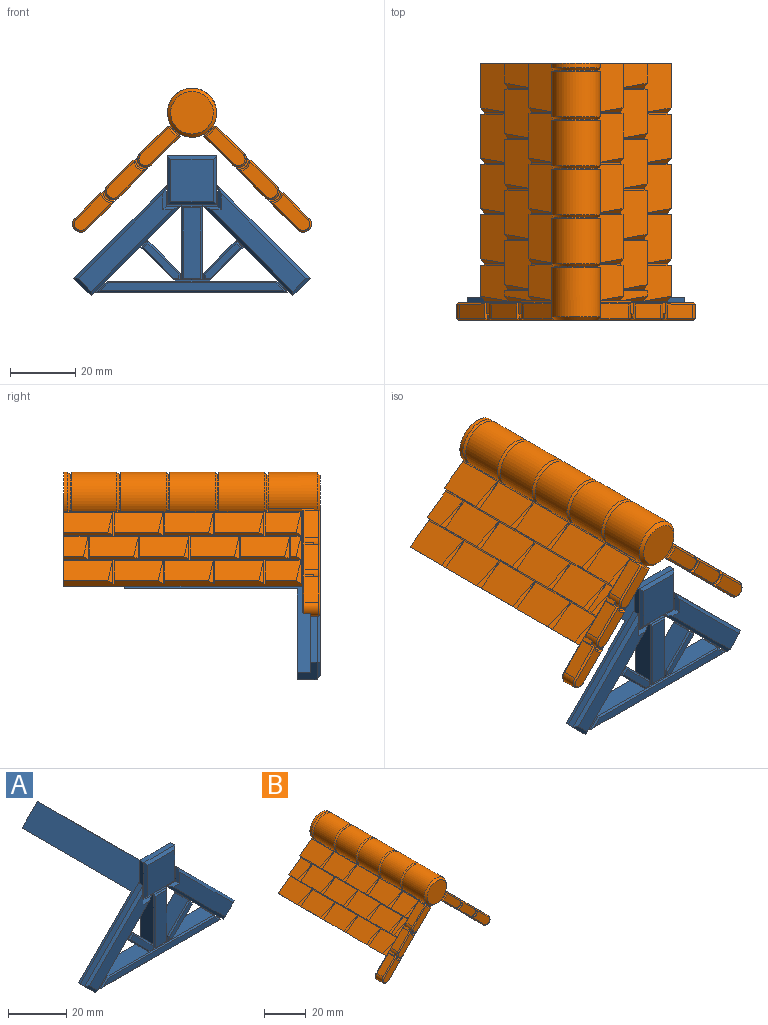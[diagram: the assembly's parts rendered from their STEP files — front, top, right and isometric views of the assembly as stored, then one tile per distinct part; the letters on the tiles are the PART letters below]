
ASSEMBLY  parts=2 mates=1
PART A: 105 faces, bbox 72.4x60x42.8 mm
  f0: plane 6x5.31mm, normal (-0.71,0,-0.71), area 27.5mm2, adj f2,f11,f12,f67,f70,f78
  f1: plane 4.4x0.4mm, normal (0,-1,0), area 1.7mm2, adj f4,f13,f50,f70
  f2: plane 66.14x27.77mm, normal (0,1,0), area 631.8mm2, adj f0,f4,f12,f17,f18,f26,f28,f31
  f3: plane 0.4x0.01mm, normal (0,1,0), area 0mm2, adj f4,f26,f50,f51
  f4: plane 59x15mm, normal (0,0,-1), area 826.6mm2, adj f1,f2,f3,f5,f7,f9,f10,f28
  f5: plane 15x2mm, normal (1,0,0), area 30mm2, adj f4,f6,f68,f82
  f6: plane 15x2mm, normal (0,0,1), area 30mm2, adj f5,f7,f68,f84
  f7: plane 15x2mm, normal (-1,0,0), area 30mm2, adj f4,f6,f68,f85
  f8: plane 13x13mm, normal (0,-1,0), area 169mm2, adj f82,f83,f84,f85
  f9: plane 6.2x0.4mm, normal (0,-1,0), area 2.5mm2, adj f4,f25,f26,f28
  f10: plane 4.4x0.4mm, normal (0,-1,0), area 1.7mm2, adj f4,f21,f54,f69
  f11: plane 28.28x28.28mm, normal (-0.71,0,0.71), area 80mm2, adj f0,f14,f67,f77
  f12: plane 27.37x27.37mm, normal (0.71,0,-0.71), area 207.4mm2, adj f0,f2,f13,f16,f23,f33,f49,f50
  f13: plane 4.4x2mm, normal (0,0,1), area 8.8mm2, adj f1,f12,f14,f81
  f14: plane 6.23x2mm, normal (1,0,0), area 12.5mm2, adj f11,f13,f67,f79
  f15: plane 29.77x28.86mm, normal (0,-1,0), area 191mm2, adj f77,f78,f79,f80,f81
  f16: plane 1.72x1.72mm, normal (0,-1,0), area 0.8mm2, adj f12,f39,f49,f60
  f17: plane 27.37x27.37mm, normal (-0.71,0,-0.71), area 206.4mm2, adj f2,f18,f21,f24,f42,f54,f55,f57
  f18: plane 6x5.31mm, normal (0.71,0,-0.71), area 25.8mm2, adj f2,f17,f19,f69,f71,f76,f86
  f19: plane 28.28x28.28mm, normal (0.71,0,0.71), area 80mm2, adj f18,f20,f71,f74
  f20: plane 6.23x2mm, normal (-1,0,0), area 12.5mm2, adj f19,f21,f71,f72
  f21: plane 4.4x2mm, normal (0,0,1), area 8.8mm2, adj f10,f17,f20,f73
  f22: plane 29.77x28.86mm, normal (0,-1,0), area 191mm2, adj f72,f73,f74,f75,f76
  f23: plane 3.98x3.41mm, normal (0,-1,0), area 1.7mm2, adj f12,f32,f33,f58,f59
  f24: plane 3.26x2.7mm, normal (0,-1,0), area 1.5mm2, adj f17,f34,f61,f63
  f25: plane 6.2x2.5mm, normal (0,0,1), area 15.5mm2, adj f9,f26,f28,f101
  f26: plane 22.91x6.5mm, normal (-1,0,0), area 141.2mm2, adj f2,f3,f9,f25,f27,f30,f51,f52
  f27: plane 6.2x2.5mm, normal (0,0,-1), area 15.5mm2, adj f26,f28,f30,f104
  f28: plane 22.9x6.5mm, normal (1,0,0), area 141.1mm2, adj f2,f4,f9,f25,f27,f30,f53,f103
  f29: plane 21.5x5.2mm, normal (0,-1,0), area 111.8mm2, adj f101,f102,f103,f104
  f30: plane 10.72x2.4mm, normal (0,-1,0), area 5.6mm2, adj f26,f27,f28,f31,f36,f37,f43,f44
  f31: plane 51.67x6.5mm, normal (0,0,1), area 293mm2, adj f2,f30,f32,f34,f56,f58,f64,f89
  f32: plane 3.41x3.41mm, normal (-0.71,0,0.71), area 12.1mm2, adj f23,f31,f33,f90
  f33: plane 59.06x6mm, normal (0,0,-1), area 352.9mm2, adj f12,f23,f32,f34,f86,f88
  f34: plane 6.5x3.41mm, normal (0.71,0,0.71), area 15.9mm2, adj f2,f24,f31,f33,f61,f63,f86,f87
  f35: plane 56.08x2.41mm, normal (0,-1,0), area 129.5mm2, adj f87,f88,f89,f90
  f36: plane 6.5x2.24mm, normal (0,0,-1), area 7.2mm2, adj f2,f30,f37,f40,f64,f100
  f37: plane 6.5x2mm, normal (1,0,0), area 6.3mm2, adj f2,f30,f36,f38,f52,f99
  f38: plane 9.98x9.98mm, normal (0.71,0,0.71), area 91.7mm2, adj f2,f37,f39,f97
  f39: plane 6.5x2.12mm, normal (-0.71,0,0.71), area 11.3mm2, adj f2,f16,f38,f40,f49,f60,f96
  f40: plane 9.86x9.86mm, normal (-0.71,0,-0.71), area 90.6mm2, adj f2,f36,f39,f98
  f41: plane 10.89x10.77mm, normal (0,-1,0), area 27.6mm2, adj f96,f97,f98,f99,f100
  f42: plane 1.85x1.85mm, normal (0,-1,0), area 0.9mm2, adj f17,f46,f55,f57
  f43: plane 2.5x2mm, normal (-1,0,0), area 5mm2, adj f30,f44,f47,f92
  f44: plane 6.5x2.24mm, normal (0,0,-1), area 7.1mm2, adj f2,f30,f43,f45,f56,f94
  f45: plane 9.86x9.86mm, normal (0.71,0,-0.71), area 90.6mm2, adj f2,f44,f46,f95
  f46: plane 6.5x2.12mm, normal (0.71,0,0.71), area 10.6mm2, adj f2,f42,f45,f47,f55,f57,f93
  f47: plane 9.98x9.98mm, normal (-0.71,0,0.71), area 91.7mm2, adj f2,f43,f46,f62,f91
  f48: plane 10.89x10.77mm, normal (0,-1,0), area 27.6mm2, adj f91,f92,f93,f94,f95
  f49: plane 4x0.27mm, normal (0.71,0,0.71), area 1.5mm2, adj f2,f12,f16,f39
  f50: plane 4x0.41mm, normal (1,0,0), area 1.6mm2, adj f1,f2,f3,f12,f51,f66
  f51: plane 4x0.4mm, normal (0,0,-1), area 1.6mm2, adj f3,f26,f50,f66
  f52: plane 4x0.4mm, normal (0,0,1), area 1.6mm2, adj f2,f26,f30,f37
  f53: plane 4x0.39mm, normal (0,0,1), area 1.6mm2, adj f2,f28,f30,f62
  f54: plane 4x0.4mm, normal (-1,0,0), area 1.6mm2, adj f2,f4,f10,f17
  f55: plane 4x0.27mm, normal (-0.71,0,0.71), area 1.5mm2, adj f2,f17,f42,f46
  f56: plane 4x0.4mm, normal (1,0,0), area 1.6mm2, adj f2,f30,f31,f44
  f57: plane 4x0.27mm, normal (0.71,0,-0.71), area 1.5mm2, adj f2,f17,f42,f46
  f58: plane 4x0.47mm, normal (-0.69,0,0.72), area 2.6mm2, adj f2,f23,f31,f59
  f59: plane 4x0.54mm, normal (0,0,1), area 2.2mm2, adj f2,f12,f23,f58
  f60: plane 4x0.27mm, normal (-0.71,0,-0.71), area 1.5mm2, adj f2,f12,f16,f39
  f61: plane 3.9x0.57mm, normal (0,0,-1), area 2.2mm2, adj f17,f24,f34,f86
  f62: plane 4x0.32mm, normal (-1,0,0.03), area 1.3mm2, adj f2,f30,f47,f53
  f63: plane 4x0.57mm, normal (0,0,1), area 2.3mm2, adj f2,f17,f24,f34
  f64: plane 4x0.4mm, normal (-1,0,0), area 1.6mm2, adj f2,f30,f31,f36
  f65: plane 15x7.5mm, normal (0,1,0), area 56.2mm2, adj f4,f69,f70
  f66: plane 0.4x0.01mm, normal (0,-1,0), area 0mm2, adj f4,f26,f50,f51
  f67: plane 31.4x28.28mm, normal (0,1,0), area 166.4mm2, adj f0,f11,f14,f70
  f68: plane 15x15mm, normal (0,1,0), area 168.7mm2, adj f5,f6,f7,f69,f70
  f69: plane 57x33.07mm, normal (0.71,0,0.71), area 749.2mm2, adj f2,f4,f10,f18,f65,f68,f70,f71
  f70: plane 57x33.07mm, normal (-0.71,0,0.71), area 749.2mm2, adj f0,f1,f2,f4,f65,f67,f68,f69
  f71: plane 31.4x28.28mm, normal (0,1,0), area 166.4mm2, adj f18,f19,f20,f69
  f72: plane 7.23x1mm, normal (-0.71,-0.71,0), area 7.8mm2, adj f20,f22,f73,f74
  f73: plane 5.4x1mm, normal (0,-0.71,0.71), area 5.2mm2, adj f21,f22,f72,f75
  f74: plane 28.28x28.28mm, normal (0.5,-0.71,0.5), area 54.2mm2, adj f19,f22,f72,f76
  f75: plane 27.37x27.37mm, normal (-0.5,-0.71,-0.5), area 52.3mm2, adj f17,f22,f73,f76
  f76: plane 5.31x5.31mm, normal (0.5,-0.71,-0.5), area 9.2mm2, adj f18,f22,f74,f75
  f77: plane 28.28x28.28mm, normal (-0.5,-0.71,0.5), area 54.2mm2, adj f11,f15,f78,f79
  f78: plane 5.31x5.31mm, normal (-0.5,-0.71,-0.5), area 9.2mm2, adj f0,f15,f77,f80
  f79: plane 7.23x1mm, normal (0.71,-0.71,0), area 7.8mm2, adj f14,f15,f77,f81
  f80: plane 27.37x27.37mm, normal (0.5,-0.71,-0.5), area 52.3mm2, adj f12,f15,f78,f81
  f81: plane 5.4x1mm, normal (0,-0.71,0.71), area 5.2mm2, adj f13,f15,f79,f80
  f82: plane 15x1mm, normal (0.71,-0.71,0), area 19.8mm2, adj f5,f8,f83,f84
  f83: plane 15x1mm, normal (0,-0.71,-0.71), area 19.8mm2, adj f4,f8,f82,f85
  f84: plane 15x1mm, normal (0,-0.71,0.71), area 19.8mm2, adj f6,f8,f82,f85
  f85: plane 15x1mm, normal (-0.71,-0.71,0), area 19.8mm2, adj f7,f8,f83,f84
  f86: plane 62.24x1.56mm, normal (0,0.71,-0.71), area 44.9mm2, adj f2,f12,f17,f18,f33,f34,f61
  f87: plane 3.62x3.41mm, normal (0.5,-0.71,0.5), area 2.9mm2, adj f34,f35,f88,f89
  f88: plane 58.49x0.5mm, normal (0,-0.71,-0.71), area 40.5mm2, adj f33,f35,f87,f90
  f89: plane 51.67x0.5mm, normal (0,-0.71,0.71), area 36.4mm2, adj f31,f35,f87,f90
  f90: plane 3.62x3.41mm, normal (-0.5,-0.71,0.5), area 2.9mm2, adj f32,f35,f88,f89
  f91: plane 10.19x9.98mm, normal (-0.5,-0.71,0.5), area 9.7mm2, adj f47,f48,f92,f93
  f92: plane 2x0.5mm, normal (-0.71,-0.71,0), area 1.2mm2, adj f43,f48,f91,f94
  f93: plane 2.12x2.12mm, normal (0.5,-0.71,0.5), area 1.8mm2, adj f46,f48,f91,f95
  f94: plane 2.24x0.5mm, normal (0,-0.71,-0.71), area 1.3mm2, adj f44,f48,f92,f95
  f95: plane 10.06x9.86mm, normal (0.5,-0.71,-0.5), area 9.6mm2, adj f45,f48,f93,f94
  f96: plane 2.12x2.12mm, normal (-0.5,-0.71,0.5), area 1.8mm2, adj f39,f41,f97,f98
  f97: plane 10.19x9.98mm, normal (0.5,-0.71,0.5), area 9.7mm2, adj f38,f41,f96,f99
  f98: plane 10.06x9.86mm, normal (-0.5,-0.71,-0.5), area 9.6mm2, adj f40,f41,f96,f100
  f99: plane 2x0.5mm, normal (0.71,-0.71,0), area 1.2mm2, adj f37,f41,f97,f100
  f100: plane 2.24x0.5mm, normal (0,-0.71,-0.71), area 1.3mm2, adj f36,f41,f98,f99
  f101: plane 6.2x0.5mm, normal (0,-0.71,0.71), area 4mm2, adj f25,f29,f102,f103
  f102: plane 22.5x0.5mm, normal (-0.71,-0.71,0), area 15.6mm2, adj f26,f29,f101,f104
  f103: plane 22.5x0.5mm, normal (0.71,-0.71,0), area 15.6mm2, adj f28,f29,f101,f104
  f104: plane 6.2x0.5mm, normal (0,-0.71,-0.71), area 4mm2, adj f27,f29,f102,f103
PART B: 262 faces, bbox 73x78.5x44 mm
  f0: cylinder r=7.5mm len=15mm, axis (0,1,0), area 460mm2, adj f14,f121,f251,f259
  f1: cylinder r=7.5mm len=15mm, axis (0,1,0), area 460mm2, adj f14,f121,f244,f249
  f2: cylinder r=7.5mm len=15mm, axis (0,1,0), area 460mm2, adj f14,f121,f237,f242
  f3: cylinder r=7.5mm len=15mm, axis (0,1,0), area 460mm2, adj f14,f121,f230,f235
  f4: cylinder r=7.5mm len=15mm, axis (0,1,0), area 43.3mm2, adj f5,f14,f121,f228
  f5: plane 58.17x34.82mm, normal (0,1,0), area 239.8mm2, adj f4,f8,f12,f14,f41,f42,f85,f86
  f6: plane 31.73x30.05mm, normal (0,1,0), area 53.4mm2, adj f8,f9,f14,f16,f35,f39,f40,f104
  f7: cylinder r=2.5mm len=4.5mm, axis (0,1,0), area 27.5mm2, adj f9,f30,f31,f99,f224,f226
  f8: plane 73x1.77mm, normal (-0.71,0,-0.71), area 173.9mm2, adj f5,f6,f14,f47,f52,f57,f60,f65
  f9: cone r=2mm half-angle=45deg, axis (0,-1,0), area 2.5mm2, adj f6,f7,f104,f226
  f10: plane 31.73x30.05mm, normal (0,1,0), area 53.4mm2, adj f12,f13,f15,f121,f139,f143,f144,f207
  f11: cylinder r=2.5mm len=4.5mm, axis (0,1,0), area 27.5mm2, adj f13,f134,f135,f202,f224,f225
  f12: plane 73x1.77mm, normal (0.71,0,-0.71), area 173.9mm2, adj f5,f10,f121,f151,f156,f161,f164,f169
  f13: cone r=2mm half-angle=45deg, axis (0,-1,0), area 2.5mm2, adj f10,f11,f207,f225
  f14: plane 73x22.06mm, normal (-0.71,0,0.71), area 151.6mm2, adj f0,f1,f2,f3,f4,f5,f6,f8
  f15: cylinder r=7.5mm len=15mm, axis (0,1,0), area 503.7mm2, adj f10,f16,f18,f38,f39,f97,f121,f122
  f16: cylinder r=7.5mm len=10.5mm, axis (0,1,0), area 10.7mm2, adj f6,f14,f15,f257
  f17: plane 13x13mm, normal (0,-1,0), area 132.7mm2, adj f97
  f18: plane 3.28x3.19mm, normal (0,-1,0), area 2mm2, adj f15,f19,f38,f39,f118
  f19: cylinder r=8mm len=3.22mm, axis (0,1,0), area 7.2mm2, adj f18,f22,f38,f115,f118,f224
  f20: plane 8.37x8.37mm, normal (-0.71,0,0.71), area 53.3mm2, adj f21,f116,f118,f119
  f21: cylinder r=2.5mm len=4.5mm, axis (0,1,0), area 18.2mm2, adj f20,f22,f29,f37,f40,f114,f120,f224
  f22: plane 8.84x8.84mm, normal (0.71,0,-0.71), area 31.2mm2, adj f19,f21,f113,f224
  f23: plane 11.79x11.79mm, normal (0,-1,0), area 53mm2, adj f113,f114,f115,f116
  f24: plane 7.82x7.82mm, normal (-0.71,0,0.71), area 49.8mm2, adj f25,f108,f110,f111
  f25: cylinder r=2.5mm len=4.5mm, axis (0,1,0), area 18.2mm2, adj f24,f26,f34,f35,f36,f106,f112,f224
  f26: plane 8.84x8.84mm, normal (0.71,0,-0.71), area 31.2mm2, adj f25,f27,f105,f224
  f27: cylinder r=2.73mm len=3.7mm, axis (0,1,0), area 8.4mm2, adj f26,f29,f37,f107,f110,f224
  f28: plane 11.24x11.24mm, normal (0,-1,0), area 48.6mm2, adj f105,f106,f107,f108
  f29: plane 3.67x3.37mm, normal (0,-1,0), area 2.7mm2, adj f21,f27,f37,f40,f110
  f30: plane 7.82x7.82mm, normal (-0.71,0,0.71), area 49.8mm2, adj f7,f101,f103,f104
  f31: plane 8.84x8.84mm, normal (0.71,0,-0.71), area 31.2mm2, adj f7,f32,f98,f224
  f32: cylinder r=2.73mm len=3.7mm, axis (0,1,0), area 8.4mm2, adj f31,f34,f36,f100,f103,f224
  f33: plane 11.24x11.24mm, normal (0,-1,0), area 48.6mm2, adj f98,f99,f100,f101
  f34: plane 3.67x3.37mm, normal (0,-1,0), area 2.7mm2, adj f25,f32,f35,f36,f103
  f35: plane 3.5x1.91mm, normal (-0.71,0,0.71), area 4.4mm2, adj f6,f25,f34,f103,f112
  f36: plane 1x0.54mm, normal (0.71,0,-0.71), area 0.8mm2, adj f25,f32,f34,f224
  f37: plane 1x0.54mm, normal (0.71,0,-0.71), area 0.8mm2, adj f21,f27,f29,f224
  f38: plane 1x0.37mm, normal (0.71,0,-0.71), area 0.5mm2, adj f15,f18,f19,f224
  f39: plane 3.5x0.45mm, normal (-0.71,0,0.71), area 2.2mm2, adj f6,f15,f18,f118
  f40: plane 3.5x1.91mm, normal (-0.71,0,0.71), area 4.4mm2, adj f6,f21,f29,f110,f120
  f41: plane 15x1.06mm, normal (-0.71,0,-0.71), area 21.4mm2, adj f5,f14,f80,f95
  f42: plane 7.5x1.06mm, normal (-0.71,0,-0.71), area 10.1mm2, adj f5,f14,f70,f86
  f43: plane 15x1.06mm, normal (-0.71,0,-0.71), area 21.4mm2, adj f14,f44,f71,f87
  f44: plane 8.13x7.07mm, normal (0,1,0), area 7.5mm2, adj f14,f43,f87
  f45: plane 8.13x7.07mm, normal (0,1,0), area 7.5mm2, adj f14,f46,f94
  f46: plane 15x1.06mm, normal (-0.71,0,-0.71), area 21.4mm2, adj f14,f45,f79,f94
  f47: plane 8.13x7.07mm, normal (0,1,0), area 7.5mm2, adj f8,f14,f84
  f48: plane 8.13x7.07mm, normal (0,1,0), area 7.5mm2, adj f14,f49,f88
  f49: plane 15x1.06mm, normal (-0.71,0,-0.71), area 21.4mm2, adj f14,f48,f72,f88
  f50: plane 8.13x7.07mm, normal (0,1,0), area 7.5mm2, adj f14,f51,f93
  f51: plane 15x1.06mm, normal (-0.71,0,-0.71), area 21.4mm2, adj f14,f50,f78,f93
  f52: plane 8.13x7.07mm, normal (0,1,0), area 7.5mm2, adj f8,f14,f83
  f53: plane 8.13x7.07mm, normal (0,1,0), area 7.5mm2, adj f14,f54,f89
  f54: plane 15x1.06mm, normal (-0.71,0,-0.71), area 21.4mm2, adj f14,f53,f73,f89
  f55: plane 8.13x7.07mm, normal (0,1,0), area 7.5mm2, adj f14,f56,f92
  f56: plane 15x1.06mm, normal (-0.71,0,-0.71), area 21.4mm2, adj f14,f55,f77,f92
  f57: plane 8.13x7.07mm, normal (0,1,0), area 7.5mm2, adj f8,f14,f82
  f58: plane 8.13x7.07mm, normal (0,1,0), area 7.5mm2, adj f14,f59,f90
  f59: plane 15x1.06mm, normal (-0.71,0,-0.71), area 21.4mm2, adj f14,f58,f74,f90
  f60: plane 8.13x7.07mm, normal (0,1,0), area 7.5mm2, adj f8,f14,f81
  f61: plane 8.13x7.07mm, normal (0,1,0), area 7.5mm2, adj f14,f62,f96
  f62: plane 3.1x1.06mm, normal (-0.71,0,-0.71), area 3.5mm2, adj f14,f61,f75,f96
  f63: plane 8.13x7.07mm, normal (0,1,0), area 7.5mm2, adj f14,f64,f91
  f64: plane 11x1.06mm, normal (-0.71,0,-0.71), area 15.4mm2, adj f14,f63,f76,f91
  f65: plane 8.13x7.07mm, normal (-0.5,-0.71,0.5), area 10.6mm2, adj f8,f14,f81
  f66: plane 8.13x7.07mm, normal (-0.5,-0.71,0.5), area 10.6mm2, adj f8,f14,f82
  f67: plane 8.13x7.07mm, normal (-0.5,-0.71,0.5), area 10.6mm2, adj f8,f14,f83
  f68: plane 8.13x7.07mm, normal (-0.5,-0.71,0.5), area 10.6mm2, adj f8,f14,f84
  f69: plane 8.13x7.07mm, normal (-0.5,-0.71,0.5), area 10.6mm2, adj f8,f14,f85
  f70: plane 8.13x7.07mm, normal (-0.5,-0.71,0.5), area 10.6mm2, adj f14,f42,f86
  f71: plane 8.13x7.07mm, normal (-0.5,-0.71,0.5), area 10.6mm2, adj f14,f43,f87
  f72: plane 8.13x7.07mm, normal (-0.5,-0.71,0.5), area 10.6mm2, adj f14,f49,f88
  f73: plane 8.13x7.07mm, normal (-0.5,-0.71,0.5), area 10.6mm2, adj f14,f54,f89
  f74: plane 8.13x7.07mm, normal (-0.5,-0.71,0.5), area 10.6mm2, adj f14,f59,f90
  f75: plane 8.13x7.07mm, normal (-0.5,-0.71,0.5), area 10.6mm2, adj f14,f62,f96
  f76: plane 8.13x7.07mm, normal (-0.5,-0.71,0.5), area 10.6mm2, adj f14,f64,f91
  f77: plane 8.13x7.07mm, normal (-0.5,-0.71,0.5), area 10.6mm2, adj f14,f56,f92
  f78: plane 8.13x7.07mm, normal (-0.5,-0.71,0.5), area 10.6mm2, adj f14,f51,f93
  f79: plane 8.13x7.07mm, normal (-0.5,-0.71,0.5), area 10.6mm2, adj f14,f46,f94
  f80: plane 8.13x7.07mm, normal (-0.5,-0.71,0.5), area 10.6mm2, adj f14,f41,f95
  f81: plane 11x8.13mm, normal (-0.59,0,0.8), area 103.6mm2, adj f8,f14,f60,f65
  f82: plane 15x8.13mm, normal (-0.59,0,0.8), area 144.1mm2, adj f8,f14,f57,f66
  f83: plane 15x8.13mm, normal (-0.59,0,0.8), area 144.1mm2, adj f8,f14,f52,f67
  f84: plane 15x8.13mm, normal (-0.59,0,0.8), area 144.1mm2, adj f8,f14,f47,f68
  f85: plane 15x8.13mm, normal (-0.59,0,0.8), area 144.1mm2, adj f5,f8,f14,f69
  f86: plane 8.13x7.5mm, normal (-0.59,0,0.8), area 68.3mm2, adj f5,f14,f42,f70
  f87: plane 15x8.13mm, normal (-0.59,0,0.8), area 144.1mm2, adj f14,f43,f44,f71
  f88: plane 15x8.13mm, normal (-0.59,0,0.8), area 144.1mm2, adj f14,f48,f49,f72
  f89: plane 15x8.13mm, normal (-0.59,0,0.8), area 144.1mm2, adj f14,f53,f54,f73
  f90: plane 15x8.13mm, normal (-0.59,0,0.8), area 144.1mm2, adj f14,f58,f59,f74
  f91: plane 11x8.13mm, normal (-0.59,0,0.8), area 103.6mm2, adj f14,f63,f64,f76
  f92: plane 15x8.13mm, normal (-0.59,0,0.8), area 144.1mm2, adj f14,f55,f56,f77
  f93: plane 15x8.13mm, normal (-0.59,0,0.8), area 144.1mm2, adj f14,f50,f51,f78
  f94: plane 15x8.13mm, normal (-0.59,0,0.8), area 144.1mm2, adj f14,f45,f46,f79
  f95: plane 15x8.13mm, normal (-0.59,0,0.8), area 144.1mm2, adj f5,f14,f41,f80
  f96: plane 8.13x6.01mm, normal (-0.59,0,0.8), area 23.8mm2, adj f14,f61,f62,f75
  f97: cone r=6.5mm half-angle=45deg, axis (0,1,0), area 62.2mm2, adj f15,f17
  f98: plane 9.19x8.84mm, normal (0.5,-0.71,-0.5), area 8.3mm2, adj f31,f33,f99,f100
  f99: cone r=2mm half-angle=45deg, axis (0,1,0), area 5mm2, adj f7,f33,f98,f101
  f100: cone r=2.73mm half-angle=45deg, axis (0,-1,0), area 3.2mm2, adj f32,f33,f98,f102
  f101: plane 8.18x8.18mm, normal (-0.5,-0.71,0.5), area 7.8mm2, adj f30,f33,f99,f102
  f102: plane 0.85x0.5mm, normal (0.3,-0.4,0.87), area 0.2mm2, adj f100,f101,f103
  f103: plane 5x0.85mm, normal (0.33,0,0.94), area 3.2mm2, adj f30,f32,f34,f35,f102,f104
  f104: plane 8.35x8.18mm, normal (-0.5,0.71,0.5), area 7.9mm2, adj f6,f9,f30,f103
  f105: plane 9.19x8.84mm, normal (0.5,-0.71,-0.5), area 8.3mm2, adj f26,f28,f106,f107
  f106: cone r=2mm half-angle=45deg, axis (0,1,0), area 5mm2, adj f25,f28,f105,f108
  f107: cone r=2.73mm half-angle=45deg, axis (0,-1,0), area 3.2mm2, adj f27,f28,f105,f109
  f108: plane 8.18x8.18mm, normal (-0.5,-0.71,0.5), area 7.8mm2, adj f24,f28,f106,f109
  f109: plane 0.85x0.5mm, normal (0.3,-0.4,0.87), area 0.2mm2, adj f107,f108,f110
  f110: plane 5x0.85mm, normal (0.33,0,0.94), area 3.2mm2, adj f24,f27,f29,f40,f109,f111
  f111: plane 8.35x8.18mm, normal (-0.5,0.71,0.5), area 7.9mm2, adj f6,f24,f110,f112
  f112: cone r=2mm half-angle=45deg, axis (0,-1,0), area 0.7mm2, adj f6,f25,f35,f111
  f113: plane 9.21x8.86mm, normal (0.5,-0.71,-0.5), area 8.6mm2, adj f22,f23,f114,f115
  f114: cone r=2mm half-angle=45deg, axis (0,1,0), area 5mm2, adj f21,f23,f113,f116
  f115: cone r=8mm half-angle=45deg, axis (0,-1,0), area 3mm2, adj f19,f23,f113,f117
  f116: plane 8.72x8.72mm, normal (-0.5,-0.71,0.5), area 8.4mm2, adj f20,f23,f114,f117
  f117: plane 0.78x0.5mm, normal (0.1,-0.53,0.84), area 0.2mm2, adj f115,f116,f118
  f118: plane 5x0.78mm, normal (0.12,0,0.99), area 3.2mm2, adj f18,f19,f20,f39,f117,f119
  f119: plane 9x8.72mm, normal (-0.5,0.71,0.5), area 8.5mm2, adj f6,f20,f118,f120
  f120: cone r=2mm half-angle=45deg, axis (0,-1,0), area 0.7mm2, adj f6,f21,f40,f119
  f121: plane 73x22.06mm, normal (0.71,0,0.71), area 151.6mm2, adj f0,f1,f2,f3,f4,f5,f10,f12
  f122: plane 3.28x3.19mm, normal (0,-1,0), area 2mm2, adj f15,f123,f142,f143,f221
  f123: cylinder r=8mm len=3.22mm, axis (0,1,0), area 7.2mm2, adj f122,f126,f142,f218,f221,f224
  f124: plane 8.37x8.37mm, normal (0.71,0,0.71), area 53.3mm2, adj f125,f219,f221,f222
  f125: cylinder r=2.5mm len=4.5mm, axis (0,1,0), area 18.2mm2, adj f124,f126,f133,f141,f144,f217,f223,f224
  f126: plane 8.84x8.84mm, normal (-0.71,0,-0.71), area 31.2mm2, adj f123,f125,f216,f224
  f127: plane 11.79x11.79mm, normal (0,-1,0), area 53mm2, adj f216,f217,f218,f219
  f128: plane 7.82x7.82mm, normal (0.71,0,0.71), area 49.8mm2, adj f129,f211,f213,f214
  f129: cylinder r=2.5mm len=4.5mm, axis (0,1,0), area 18.2mm2, adj f128,f130,f138,f139,f140,f209,f215,f224
  f130: plane 8.84x8.84mm, normal (-0.71,0,-0.71), area 31.2mm2, adj f129,f131,f208,f224
  f131: cylinder r=2.73mm len=3.7mm, axis (0,1,0), area 8.4mm2, adj f130,f133,f141,f210,f213,f224
  f132: plane 11.24x11.24mm, normal (0,-1,0), area 48.6mm2, adj f208,f209,f210,f211
  f133: plane 3.67x3.37mm, normal (0,-1,0), area 2.7mm2, adj f125,f131,f141,f144,f213
  f134: plane 7.82x7.82mm, normal (0.71,0,0.71), area 49.8mm2, adj f11,f204,f206,f207
  f135: plane 8.84x8.84mm, normal (-0.71,0,-0.71), area 31.2mm2, adj f11,f136,f201,f224
  f136: cylinder r=2.73mm len=3.7mm, axis (0,1,0), area 8.4mm2, adj f135,f138,f140,f203,f206,f224
  f137: plane 11.24x11.24mm, normal (0,-1,0), area 48.6mm2, adj f201,f202,f203,f204
  f138: plane 3.67x3.37mm, normal (0,-1,0), area 2.7mm2, adj f129,f136,f139,f140,f206
  f139: plane 3.5x1.91mm, normal (0.71,0,0.71), area 4.4mm2, adj f10,f129,f138,f206,f215
  f140: plane 1x0.54mm, normal (-0.71,0,-0.71), area 0.8mm2, adj f129,f136,f138,f224
  f141: plane 1x0.54mm, normal (-0.71,0,-0.71), area 0.8mm2, adj f125,f131,f133,f224
  f142: plane 1x0.37mm, normal (-0.71,0,-0.71), area 0.5mm2, adj f15,f122,f123,f224
  f143: plane 3.5x0.45mm, normal (0.71,0,0.71), area 2.2mm2, adj f10,f15,f122,f221
  f144: plane 3.5x1.91mm, normal (0.71,0,0.71), area 4.4mm2, adj f10,f125,f133,f213,f223
  f145: plane 15x1.06mm, normal (0.71,0,-0.71), area 21.4mm2, adj f5,f121,f184,f199
  f146: plane 7.5x1.06mm, normal (0.71,0,-0.71), area 10.1mm2, adj f5,f121,f174,f190
  f147: plane 15x1.06mm, normal (0.71,0,-0.71), area 21.4mm2, adj f121,f148,f175,f191
  f148: plane 8.13x7.07mm, normal (0,1,0), area 7.5mm2, adj f121,f147,f191
  f149: plane 8.13x7.07mm, normal (0,1,0), area 7.5mm2, adj f121,f150,f198
  f150: plane 15x1.06mm, normal (0.71,0,-0.71), area 21.4mm2, adj f121,f149,f183,f198
  f151: plane 8.13x7.07mm, normal (0,1,0), area 7.5mm2, adj f12,f121,f188
  f152: plane 8.13x7.07mm, normal (0,1,0), area 7.5mm2, adj f121,f153,f192
  f153: plane 15x1.06mm, normal (0.71,0,-0.71), area 21.4mm2, adj f121,f152,f176,f192
  f154: plane 8.13x7.07mm, normal (0,1,0), area 7.5mm2, adj f121,f155,f197
  f155: plane 15x1.06mm, normal (0.71,0,-0.71), area 21.4mm2, adj f121,f154,f182,f197
  f156: plane 8.13x7.07mm, normal (0,1,0), area 7.5mm2, adj f12,f121,f187
  f157: plane 8.13x7.07mm, normal (0,1,0), area 7.5mm2, adj f121,f158,f193
  f158: plane 15x1.06mm, normal (0.71,0,-0.71), area 21.4mm2, adj f121,f157,f177,f193
  f159: plane 8.13x7.07mm, normal (0,1,0), area 7.5mm2, adj f121,f160,f196
  f160: plane 15x1.06mm, normal (0.71,0,-0.71), area 21.4mm2, adj f121,f159,f181,f196
  f161: plane 8.13x7.07mm, normal (0,1,0), area 7.5mm2, adj f12,f121,f186
  f162: plane 8.13x7.07mm, normal (0,1,0), area 7.5mm2, adj f121,f163,f194
  f163: plane 15x1.06mm, normal (0.71,0,-0.71), area 21.4mm2, adj f121,f162,f178,f194
  f164: plane 8.13x7.07mm, normal (0,1,0), area 7.5mm2, adj f12,f121,f185
  f165: plane 8.13x7.07mm, normal (0,1,0), area 7.5mm2, adj f121,f166,f200
  f166: plane 3.1x1.06mm, normal (0.71,0,-0.71), area 3.5mm2, adj f121,f165,f179,f200
  f167: plane 8.13x7.07mm, normal (0,1,0), area 7.5mm2, adj f121,f168,f195
  f168: plane 11x1.06mm, normal (0.71,0,-0.71), area 15.4mm2, adj f121,f167,f180,f195
  f169: plane 8.13x7.07mm, normal (0.5,-0.71,0.5), area 10.6mm2, adj f12,f121,f185
  f170: plane 8.13x7.07mm, normal (0.5,-0.71,0.5), area 10.6mm2, adj f12,f121,f186
  f171: plane 8.13x7.07mm, normal (0.5,-0.71,0.5), area 10.6mm2, adj f12,f121,f187
  f172: plane 8.13x7.07mm, normal (0.5,-0.71,0.5), area 10.6mm2, adj f12,f121,f188
  f173: plane 8.13x7.07mm, normal (0.5,-0.71,0.5), area 10.6mm2, adj f12,f121,f189
  f174: plane 8.13x7.07mm, normal (0.5,-0.71,0.5), area 10.6mm2, adj f121,f146,f190
  f175: plane 8.13x7.07mm, normal (0.5,-0.71,0.5), area 10.6mm2, adj f121,f147,f191
  f176: plane 8.13x7.07mm, normal (0.5,-0.71,0.5), area 10.6mm2, adj f121,f153,f192
  f177: plane 8.13x7.07mm, normal (0.5,-0.71,0.5), area 10.6mm2, adj f121,f158,f193
  f178: plane 8.13x7.07mm, normal (0.5,-0.71,0.5), area 10.6mm2, adj f121,f163,f194
  f179: plane 8.13x7.07mm, normal (0.5,-0.71,0.5), area 10.6mm2, adj f121,f166,f200
  f180: plane 8.13x7.07mm, normal (0.5,-0.71,0.5), area 10.6mm2, adj f121,f168,f195
  f181: plane 8.13x7.07mm, normal (0.5,-0.71,0.5), area 10.6mm2, adj f121,f160,f196
  f182: plane 8.13x7.07mm, normal (0.5,-0.71,0.5), area 10.6mm2, adj f121,f155,f197
  f183: plane 8.13x7.07mm, normal (0.5,-0.71,0.5), area 10.6mm2, adj f121,f150,f198
  f184: plane 8.13x7.07mm, normal (0.5,-0.71,0.5), area 10.6mm2, adj f121,f145,f199
  f185: plane 11x8.13mm, normal (0.59,0,0.8), area 103.6mm2, adj f12,f121,f164,f169
  f186: plane 15x8.13mm, normal (0.59,0,0.8), area 144.1mm2, adj f12,f121,f161,f170
  f187: plane 15x8.13mm, normal (0.59,0,0.8), area 144.1mm2, adj f12,f121,f156,f171
  f188: plane 15x8.13mm, normal (0.59,0,0.8), area 144.1mm2, adj f12,f121,f151,f172
  f189: plane 15x8.13mm, normal (0.59,0,0.8), area 144.1mm2, adj f5,f12,f121,f173
  f190: plane 8.13x7.5mm, normal (0.59,0,0.8), area 68.3mm2, adj f5,f121,f146,f174
  f191: plane 15x8.13mm, normal (0.59,0,0.8), area 144.1mm2, adj f121,f147,f148,f175
  f192: plane 15x8.13mm, normal (0.59,0,0.8), area 144.1mm2, adj f121,f152,f153,f176
  f193: plane 15x8.13mm, normal (0.59,0,0.8), area 144.1mm2, adj f121,f157,f158,f177
  f194: plane 15x8.13mm, normal (0.59,0,0.8), area 144.1mm2, adj f121,f162,f163,f178
  f195: plane 11x8.13mm, normal (0.59,0,0.8), area 103.6mm2, adj f121,f167,f168,f180
  f196: plane 15x8.13mm, normal (0.59,0,0.8), area 144.1mm2, adj f121,f159,f160,f181
  f197: plane 15x8.13mm, normal (0.59,0,0.8), area 144.1mm2, adj f121,f154,f155,f182
  f198: plane 15x8.13mm, normal (0.59,0,0.8), area 144.1mm2, adj f121,f149,f150,f183
  f199: plane 15x8.13mm, normal (0.59,0,0.8), area 144.1mm2, adj f5,f121,f145,f184
  f200: plane 8.13x6.01mm, normal (0.59,0,0.8), area 23.8mm2, adj f121,f165,f166,f179
  f201: plane 9.19x8.84mm, normal (-0.5,-0.71,-0.5), area 8.3mm2, adj f135,f137,f202,f203
  f202: cone r=2mm half-angle=45deg, axis (0,1,0), area 5mm2, adj f11,f137,f201,f204
  f203: cone r=2.73mm half-angle=45deg, axis (0,-1,0), area 3.2mm2, adj f136,f137,f201,f205
  f204: plane 8.18x8.18mm, normal (0.5,-0.71,0.5), area 7.8mm2, adj f134,f137,f202,f205
  f205: plane 0.85x0.5mm, normal (-0.3,-0.4,0.87), area 0.2mm2, adj f203,f204,f206
  f206: plane 5x0.85mm, normal (-0.33,0,0.94), area 3.2mm2, adj f134,f136,f138,f139,f205,f207
  f207: plane 8.35x8.18mm, normal (0.5,0.71,0.5), area 7.9mm2, adj f10,f13,f134,f206
  f208: plane 9.19x8.84mm, normal (-0.5,-0.71,-0.5), area 8.3mm2, adj f130,f132,f209,f210
  f209: cone r=2mm half-angle=45deg, axis (0,1,0), area 5mm2, adj f129,f132,f208,f211
  f210: cone r=2.73mm half-angle=45deg, axis (0,-1,0), area 3.2mm2, adj f131,f132,f208,f212
  f211: plane 8.18x8.18mm, normal (0.5,-0.71,0.5), area 7.8mm2, adj f128,f132,f209,f212
  f212: plane 0.85x0.5mm, normal (-0.3,-0.4,0.87), area 0.2mm2, adj f210,f211,f213
  f213: plane 5x0.85mm, normal (-0.33,0,0.94), area 3.2mm2, adj f128,f131,f133,f144,f212,f214
  f214: plane 8.35x8.18mm, normal (0.5,0.71,0.5), area 7.9mm2, adj f10,f128,f213,f215
  f215: cone r=2mm half-angle=45deg, axis (0,-1,0), area 0.7mm2, adj f10,f129,f139,f214
  f216: plane 9.21x8.86mm, normal (-0.5,-0.71,-0.5), area 8.6mm2, adj f126,f127,f217,f218
  f217: cone r=2mm half-angle=45deg, axis (0,1,0), area 5mm2, adj f125,f127,f216,f219
  f218: cone r=8mm half-angle=45deg, axis (0,-1,0), area 3mm2, adj f123,f127,f216,f220
  f219: plane 8.72x8.72mm, normal (0.5,-0.71,0.5), area 8.4mm2, adj f124,f127,f217,f220
  f220: plane 0.78x0.5mm, normal (-0.1,-0.53,0.84), area 0.2mm2, adj f218,f219,f221
  f221: plane 5x0.78mm, normal (-0.12,0,0.99), area 3.2mm2, adj f122,f123,f124,f143,f220,f222
  f222: plane 9x8.72mm, normal (0.5,0.71,0.5), area 8.5mm2, adj f10,f124,f221,f223
  f223: cone r=2mm half-angle=45deg, axis (0,-1,0), area 0.7mm2, adj f10,f125,f144,f222
  f224: plane 71.56x36.51mm, normal (0,1,0), area 255.4mm2, adj f7,f11,f15,f19,f21,f22,f25,f26
  f225: plane 75.5x35.78mm, normal (-0.71,0,-0.71), area 2946.6mm2, adj f5,f10,f11,f12,f13,f224,f226
  f226: plane 75.5x35.78mm, normal (0.71,0,-0.71), area 2946.6mm2, adj f5,f6,f7,f8,f9,f224,f225
  f227: cylinder r=7.5mm len=1.2mm, axis (0,-1,0), area 0mm2, adj f14,f228,f230,f233
  f228: cone r=6.7mm half-angle=45deg, axis (0,1,0), area 35.8mm2, adj f4,f227,f229,f231,f232,f233
  f229: cylinder r=7.5mm len=1.2mm, axis (0,-1,0), area 0mm2, adj f121,f228,f230,f232
  f230: plane 15x12.07mm, normal (0,1,0), area 25.3mm2, adj f3,f227,f229,f231,f232,f233
  f231: cylinder r=6.7mm len=13.4mm, axis (0,-1,0), area 11.9mm2, adj f228,f230,f232,f233
  f232: plane 1.2x0.63mm, normal (0.61,0,0.79), area 0.6mm2, adj f228,f229,f230,f231
  f233: plane 1.2x0.63mm, normal (-0.61,0,0.79), area 0.6mm2, adj f227,f228,f230,f231
  f234: cylinder r=7.5mm len=1.2mm, axis (0,-1,0), area 0mm2, adj f14,f235,f237,f240
  f235: cone r=6.7mm half-angle=45deg, axis (0,1,0), area 35.8mm2, adj f3,f234,f236,f238,f239,f240
  f236: cylinder r=7.5mm len=1.2mm, axis (0,-1,0), area 0mm2, adj f121,f235,f237,f239
  f237: plane 15x12.07mm, normal (0,1,0), area 25.3mm2, adj f2,f234,f236,f238,f239,f240
  f238: cylinder r=6.7mm len=13.4mm, axis (0,-1,0), area 11.9mm2, adj f235,f237,f239,f240
  f239: plane 1.2x0.63mm, normal (0.61,0,0.79), area 0.6mm2, adj f235,f236,f237,f238
  f240: plane 1.2x0.63mm, normal (-0.61,0,0.79), area 0.6mm2, adj f234,f235,f237,f238
  f241: cylinder r=7.5mm len=1.2mm, axis (0,-1,0), area 0mm2, adj f14,f242,f244,f247
  f242: cone r=6.7mm half-angle=45deg, axis (0,1,0), area 35.8mm2, adj f2,f241,f243,f245,f246,f247
  f243: cylinder r=7.5mm len=1.2mm, axis (0,-1,0), area 0mm2, adj f121,f242,f244,f246
  f244: plane 15x12.07mm, normal (0,1,0), area 25.3mm2, adj f1,f241,f243,f245,f246,f247
  f245: cylinder r=6.7mm len=13.4mm, axis (0,-1,0), area 11.9mm2, adj f242,f244,f246,f247
  f246: plane 1.2x0.63mm, normal (0.61,0,0.79), area 0.6mm2, adj f242,f243,f244,f245
  f247: plane 1.2x0.63mm, normal (-0.61,0,0.79), area 0.6mm2, adj f241,f242,f244,f245
  f248: cylinder r=7.5mm len=1.2mm, axis (0,-1,0), area 0mm2, adj f14,f249,f251,f254
  f249: cone r=6.7mm half-angle=45deg, axis (0,1,0), area 35.8mm2, adj f1,f248,f250,f252,f253,f254
  f250: cylinder r=7.5mm len=1.2mm, axis (0,-1,0), area 0mm2, adj f121,f249,f251,f253
  f251: plane 15x12.07mm, normal (0,1,0), area 25.3mm2, adj f0,f248,f250,f252,f253,f254
  f252: cylinder r=6.7mm len=13.4mm, axis (0,-1,0), area 11.9mm2, adj f249,f251,f253,f254
  f253: plane 1.2x0.63mm, normal (0.61,0,0.79), area 0.6mm2, adj f249,f250,f251,f252
  f254: plane 1.2x0.63mm, normal (-0.61,0,0.79), area 0.6mm2, adj f248,f249,f251,f252
  f255: cylinder r=7.5mm len=1.2mm, axis (0,-1,0), area 0mm2, adj f14,f257,f259,f261
  f256: cylinder r=7.5mm len=1.2mm, axis (0,-1,0), area 0mm2, adj f121,f257,f259,f260
  f257: plane 15x12.07mm, normal (0,1,0), area 25.3mm2, adj f15,f16,f255,f256,f258,f260,f261
  f258: cylinder r=6.7mm len=13.4mm, axis (0,-1,0), area 11.9mm2, adj f257,f259,f260,f261
  f259: cone r=6.7mm half-angle=45deg, axis (0,1,0), area 35.8mm2, adj f0,f255,f256,f258,f260,f261
  f260: plane 1.2x0.63mm, normal (0.61,0,0.79), area 0.6mm2, adj f256,f257,f258,f259
  f261: plane 1.2x0.63mm, normal (-0.61,0,0.79), area 0.6mm2, adj f255,f257,f258,f259
PLACE A at identity
PLACE B t=(0,0,-31.09)mm
MATE planar B.f0 <-> A.f8  axis (0,-1,0) through (0,-3,20.7)mm
